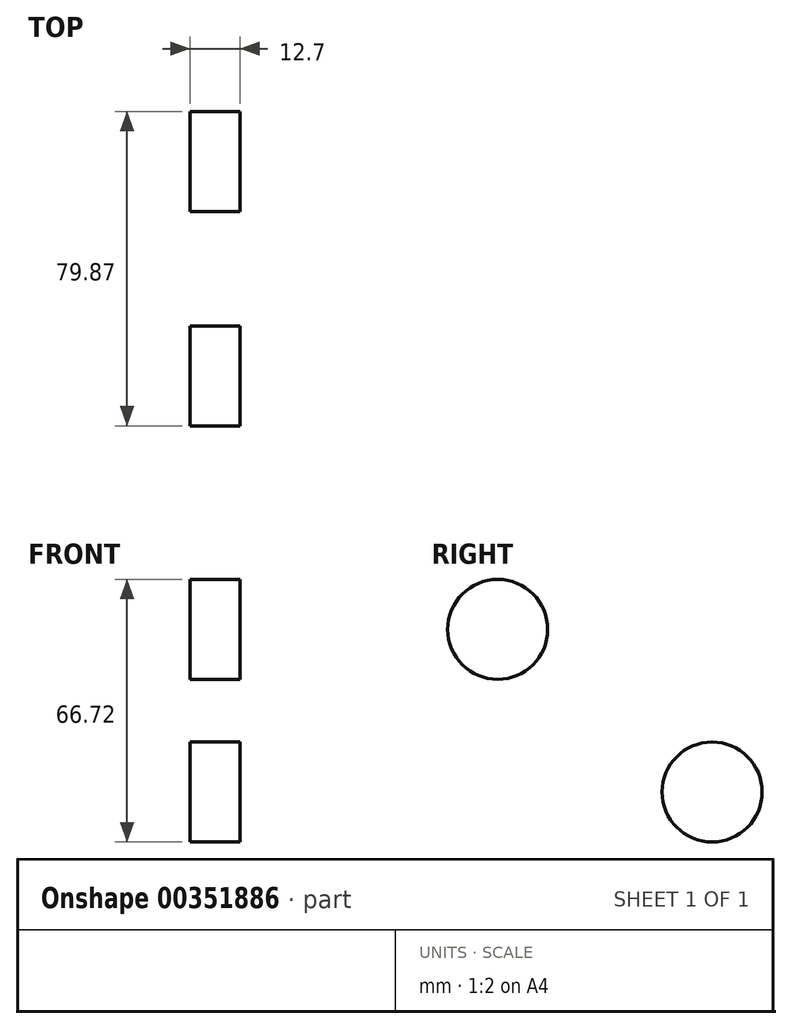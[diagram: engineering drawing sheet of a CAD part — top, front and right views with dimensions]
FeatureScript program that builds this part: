
annotation { "Feature Type Name" : "Feature", "Feature Type Description" : "" }
export const myFeature = defineFeature(function(context is Context, id is Id, definition is map)
    precondition{}
    {
        {
            var Q0;
            Q0=qCreatedBy(makeId("Right.planeOp"),FACE);
            var sketch = newSketch(context, id + "F0", { "sketchPlane" : qUnion([Q0])});
            skCircle(sketch, "E0", {"center": v(0, 0) * mm, "radius": 12.7 * mm});
            skCircle(sketch, "E1", {"center": v(-54.47, 41.32) * mm, "radius": 12.7 * mm});
            skSolve(sketch);
        }
        {
            var Q0;
            Q0=makeQuery(id+"F0.imprint","IMPRINT",FACE,{"disambiguationData":[TD([[makeQuery(id+"F0.imprint","IMPRINT",EDGE,{"derivedFrom":sQuery(id+"F0.wireOp",EDGE,"E0")}),1.0]])]});
            var Q1;
            Q1=makeQuery(id+"F0.imprint","IMPRINT",FACE,{"disambiguationData":[TD([[makeQuery(id+"F0.imprint","IMPRINT",EDGE,{"derivedFrom":sQuery(id+"F0.wireOp",EDGE,"E1")}),1.0]])]});
            extrude(context, id + "F1", {"entities" : qUnion([Q0, Q1]), "depth" : 12.7 * mm});
        }
    });
